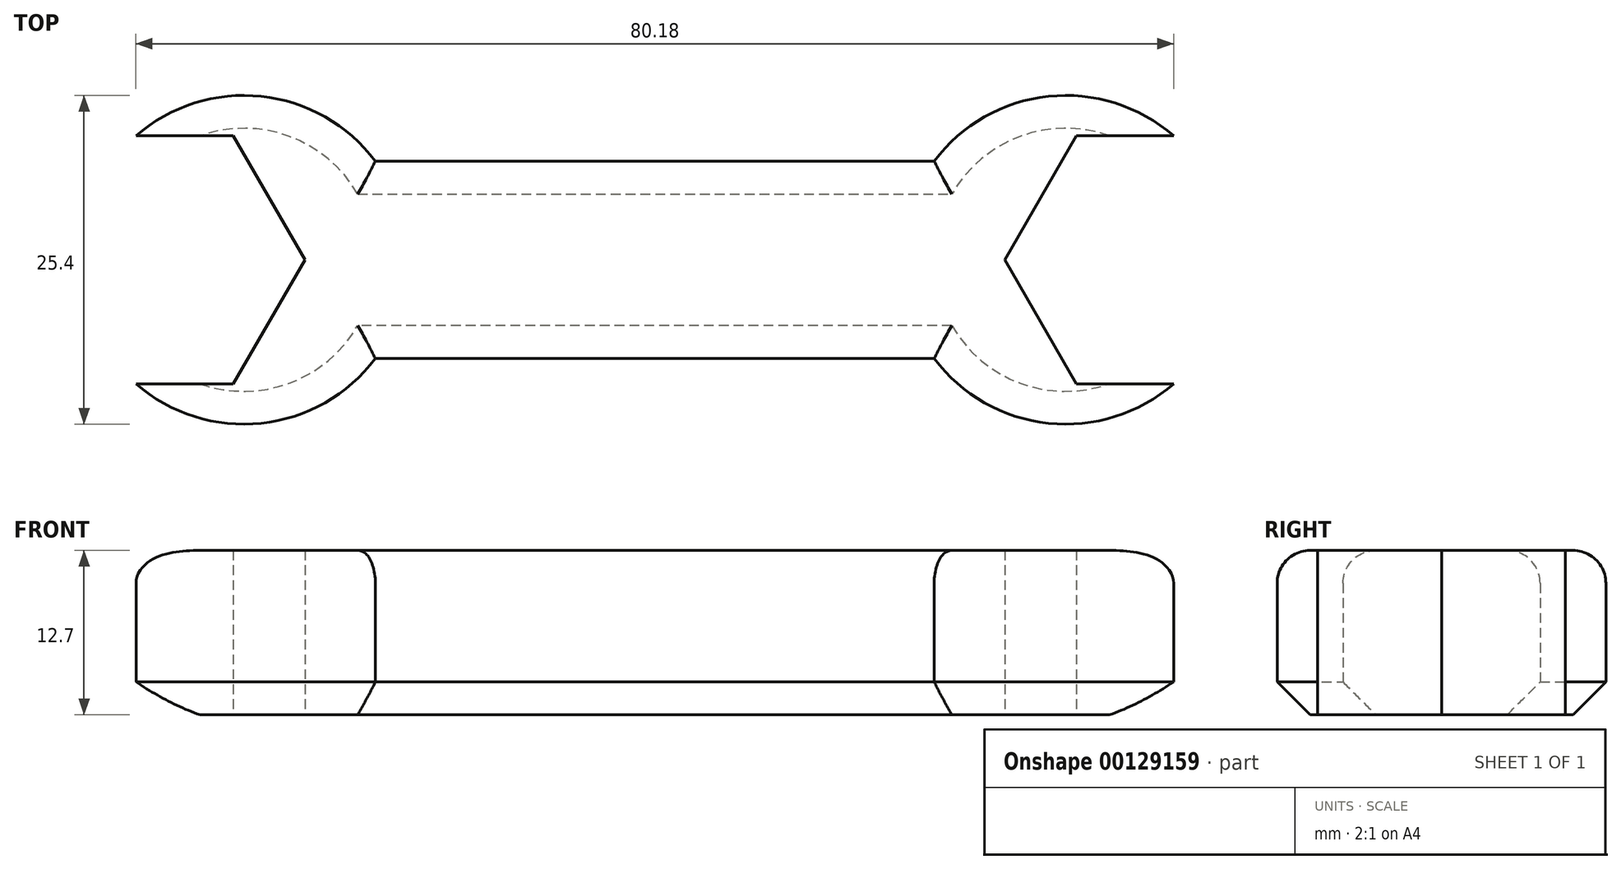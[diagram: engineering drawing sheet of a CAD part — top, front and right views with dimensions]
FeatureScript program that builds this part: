
annotation { "Feature Type Name" : "Feature", "Feature Type Description" : "" }
export const myFeature = defineFeature(function(context is Context, id is Id, definition is map)
    precondition{}
    {
        {
            var Q0;
            Q0=qCreatedBy(makeId("Top.planeOp"),FACE);
            var sketch = newSketch(context, id + "F0", { "sketchPlane" : qUnion([Q0])});
            skArc(sketch, "E0", {"start": v(-21.59, 7.62) * mm, "mid": v(-44.45, 0) * mm, "end": v(-21.6, -7.62) * mm});
            skArc(sketch, "E1", {"start": v(21.6, -7.62) * mm, "mid": v(44.45, 0) * mm, "end": v(21.59, 7.62) * mm});
            skLineSegment(sketch, "E2", {"start": v(-21.59, 7.62) * mm, "end": v(21.59, 7.62) * mm});
            skLineSegment(sketch, "E3", {"start": v(-21.59, -7.62) * mm, "end": v(21.59, -7.62) * mm});
            skLineSegment(sketch, "E4", {"start": v(-31.75, 0) * mm, "end": v(31.75, 0) * mm, "construction": true});
            skSolve(sketch);
        }
        {
            var Q0;
            Q0 = qSketchRegion(id + "F0", true);
            extrude(context, id + "F1", {"entities" : qUnion([Q0]), "endBound" : BoundingType.SYMMETRIC, "depth" : 12.7 * mm});
        }
        {
            var Q0;
            Q0=makeQuery(id+"F1.opExtrude","CAP_FACE",FACE,{"disambiguationData":[OSD([sQuery(id+"F0.wireOp",EDGE,"E0"),sQuery(id+"F0.wireOp",EDGE,"E1"),sQuery(id+"F0.wireOp",EDGE,"E2"),sQuery(id+"F0.wireOp",EDGE,"E3")])],"isStart":true});
            var sketch = newSketch(context, id + "F2", { "sketchPlane" : qUnion([Q0])});
            skCircle(sketch, "E5.cCircle", {"center": v(-38.1, 0) * mm, "radius": 9.58 * mm, "construction": true});
            skLineSegment(sketch, "E5.0", {"start": v(-49.16, 0) * mm, "end": v(-43.63, 9.58) * mm});
            skLineSegment(sketch, "E5.1", {"start": v(-43.63, 9.58) * mm, "end": v(-32.57, 9.58) * mm});
            skLineSegment(sketch, "E5.2", {"start": v(-32.57, 9.58) * mm, "end": v(-27.04, 0) * mm});
            skLineSegment(sketch, "E5.3", {"start": v(-27.04, 0) * mm, "end": v(-32.57, -9.58) * mm});
            skLineSegment(sketch, "E5.4", {"start": v(-32.57, -9.58) * mm, "end": v(-43.63, -9.58) * mm});
            skLineSegment(sketch, "E5.5", {"start": v(-43.63, -9.58) * mm, "end": v(-49.16, 0) * mm});
            skSolve(sketch);
        }
        {
            var Q0;
            Q0 = qSketchRegion(id + "F2", true);
            extrude(context, id + "F3", {"entities" : qUnion([Q0]), "endBound" : BoundingType.THROUGH_ALL, "oppositeDirection" : true, "depth" : 25.4 * mm});
        }
        {
            var Q0;
            Q0=makeQuery(id+"F3.opExtrude","SWEPT_BODY",BODY,{"disambiguationData":[OSD([sQuery(id+"F2.wireOp",EDGE,"E5.0"),sQuery(id+"F2.wireOp",EDGE,"E5.1"),sQuery(id+"F2.wireOp",EDGE,"E5.2"),sQuery(id+"F2.wireOp",EDGE,"E5.3"),sQuery(id+"F2.wireOp",EDGE,"E5.4"),sQuery(id+"F2.wireOp",EDGE,"E5.5")])]});
            var Q1;
            Q1=qCreatedBy(makeId("Right.planeOp"),FACE);
            mirror(context, id + "F4", {"operationType" : NewBodyOperationType.REMOVE, "entities" : qUnion([Q0]), "mirrorPlane" : qUnion([Q1])});
        }
        {
            var Q0;
            Q0=makeQuery(id+"F3.opExtrude","SWEPT_BODY",BODY,{"disambiguationData":[OSD([sQuery(id+"F2.wireOp",EDGE,"E5.0"),sQuery(id+"F2.wireOp",EDGE,"E5.1"),sQuery(id+"F2.wireOp",EDGE,"E5.2"),sQuery(id+"F2.wireOp",EDGE,"E5.3"),sQuery(id+"F2.wireOp",EDGE,"E5.4"),sQuery(id+"F2.wireOp",EDGE,"E5.5")])]});
            var Q1;
            Q1=makeQuery(id+"F1.opExtrude","SWEPT_BODY",BODY,{"disambiguationData":[OSD([sQuery(id+"F0.wireOp",EDGE,"E0"),sQuery(id+"F0.wireOp",EDGE,"E1"),sQuery(id+"F0.wireOp",EDGE,"E2"),sQuery(id+"F0.wireOp",EDGE,"E3")])]});
            booleanBodies(context, id + "F5", {"operationType" : BooleanOperationType.SUBTRACTION, "tools" : qUnion([Q0]), "targets" : qUnion([Q1])});
        }
        {
            var Q0;
            Q0=makeQuery(id+"F1.opExtrude","CAP_EDGE",EDGE,{"disambiguationData":[OSD([sQuery(id+"F0.wireOp",EDGE,"E3")])],"isStart":false});
            var Q1;
            {var subQ0=sQuery(id+"F0.wireOp",EDGE,"E0");var subQ1=sQuery(id+"F0.wireOp",EDGE,"E3");Q1=makeQuery(id+"F5.opBoolean","SPLIT",EDGE,{"disambiguationData":[TD([makeQuery(id+"F1.opExtrude","SWEPT_FACE",FACE,{"disambiguationData":[OSD([subQ1])]})])],"derivedFrom":makeQuery(id+"F1.opExtrude","CAP_EDGE",EDGE,{"disambiguationData":[OSD([subQ0])],"isStart":false})});}
            var Q2;
            {var subQ0=sQuery(id+"F0.wireOp",EDGE,"E0");var subQ1=sQuery(id+"F0.wireOp",EDGE,"E2");Q2=makeQuery(id+"F5.opBoolean","SPLIT",EDGE,{"disambiguationData":[TD([makeQuery(id+"F1.opExtrude","SWEPT_FACE",FACE,{"disambiguationData":[OSD([subQ1])]})])],"derivedFrom":makeQuery(id+"F1.opExtrude","CAP_EDGE",EDGE,{"disambiguationData":[OSD([subQ0])],"isStart":false})});}
            var Q3;
            Q3=makeQuery(id+"F1.opExtrude","CAP_EDGE",EDGE,{"disambiguationData":[OSD([sQuery(id+"F0.wireOp",EDGE,"E2")])],"isStart":false});
            var Q4;
            {var subQ0=sQuery(id+"F0.wireOp",EDGE,"E2");var subQ1=sQuery(id+"F0.wireOp",EDGE,"E1");Q4=makeQuery(id+"F4.boolean.opBoolean","SPLIT",EDGE,{"disambiguationData":[TD([makeQuery(id+"F1.opExtrude","SWEPT_FACE",FACE,{"disambiguationData":[OSD([subQ0])]})])],"derivedFrom":makeQuery(id+"F1.opExtrude","CAP_EDGE",EDGE,{"disambiguationData":[OSD([subQ1])],"isStart":false})});}
            var Q5;
            {var subQ0=sQuery(id+"F0.wireOp",EDGE,"E3");var subQ1=sQuery(id+"F0.wireOp",EDGE,"E1");Q5=makeQuery(id+"F4.boolean.opBoolean","SPLIT",EDGE,{"disambiguationData":[TD([makeQuery(id+"F1.opExtrude","SWEPT_FACE",FACE,{"disambiguationData":[OSD([subQ0])]})])],"derivedFrom":makeQuery(id+"F1.opExtrude","CAP_EDGE",EDGE,{"disambiguationData":[OSD([subQ1])],"isStart":false})});}
            fillet(context, id + "F6", {"entities" : qUnion([Q0, Q1, Q2, Q3, Q4, Q5]), "radius" : 2.54 * mm, "tangentPropagation" : true, "allowEdgeOverflow" : false});
        }
        {
            var Q0;
            {var subQ0=sQuery(id+"F0.wireOp",EDGE,"E3");var subQ1=sQuery(id+"F0.wireOp",EDGE,"E1");Q0=makeQuery(id+"F4.boolean.opBoolean","SPLIT",EDGE,{"disambiguationData":[TD([makeQuery(id+"F1.opExtrude","SWEPT_FACE",FACE,{"disambiguationData":[OSD([subQ0])]})])],"derivedFrom":makeQuery(id+"F1.opExtrude","CAP_EDGE",EDGE,{"disambiguationData":[OSD([subQ1])],"isStart":true})});}
            var Q1;
            {var subQ0=sQuery(id+"F0.wireOp",EDGE,"E2");var subQ1=sQuery(id+"F0.wireOp",EDGE,"E1");Q1=makeQuery(id+"F4.boolean.opBoolean","SPLIT",EDGE,{"disambiguationData":[TD([makeQuery(id+"F1.opExtrude","SWEPT_FACE",FACE,{"disambiguationData":[OSD([subQ0])]})])],"derivedFrom":makeQuery(id+"F1.opExtrude","CAP_EDGE",EDGE,{"disambiguationData":[OSD([subQ1])],"isStart":true})});}
            var Q2;
            Q2=makeQuery(id+"F1.opExtrude","CAP_EDGE",EDGE,{"disambiguationData":[OSD([sQuery(id+"F0.wireOp",EDGE,"E3")])],"isStart":true});
            var Q3;
            Q3=makeQuery(id+"F1.opExtrude","CAP_EDGE",EDGE,{"disambiguationData":[OSD([sQuery(id+"F0.wireOp",EDGE,"E2")])],"isStart":true});
            var Q4;
            {var subQ0=sQuery(id+"F0.wireOp",EDGE,"E0");var subQ1=sQuery(id+"F0.wireOp",EDGE,"E3");Q4=makeQuery(id+"F5.opBoolean","SPLIT",EDGE,{"disambiguationData":[TD([makeQuery(id+"F1.opExtrude","SWEPT_FACE",FACE,{"disambiguationData":[OSD([subQ1])]})])],"derivedFrom":makeQuery(id+"F1.opExtrude","CAP_EDGE",EDGE,{"disambiguationData":[OSD([subQ0])],"isStart":true})});}
            var Q5;
            {var subQ0=sQuery(id+"F0.wireOp",EDGE,"E0");var subQ1=sQuery(id+"F0.wireOp",EDGE,"E2");Q5=makeQuery(id+"F5.opBoolean","SPLIT",EDGE,{"disambiguationData":[TD([makeQuery(id+"F1.opExtrude","SWEPT_FACE",FACE,{"disambiguationData":[OSD([subQ1])]})])],"derivedFrom":makeQuery(id+"F1.opExtrude","CAP_EDGE",EDGE,{"disambiguationData":[OSD([subQ0])],"isStart":true})});}
            chamfer(context, id + "F7", {"entities" : qUnion([Q0, Q1, Q2, Q3, Q4, Q5]), "width" : 2.54 * mm, "tangentPropagation" : true});
        }
    });
